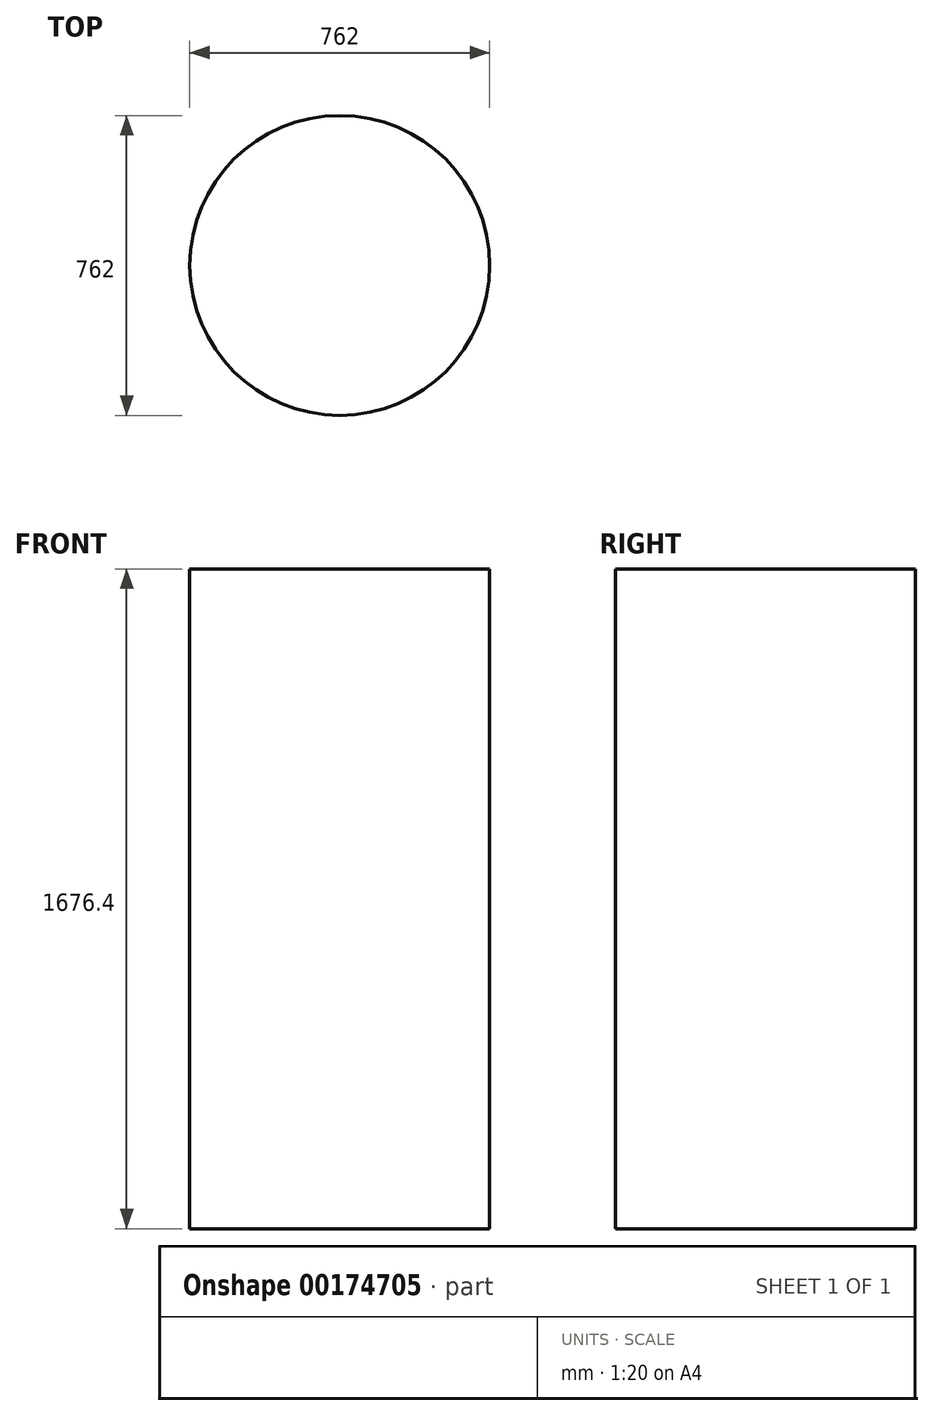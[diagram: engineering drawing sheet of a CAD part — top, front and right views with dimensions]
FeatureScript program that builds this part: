
annotation { "Feature Type Name" : "Feature", "Feature Type Description" : "" }
export const myFeature = defineFeature(function(context is Context, id is Id, definition is map)
    precondition{}
    {
        {
            var Q0;
            Q0=qCreatedBy(makeId("Top.planeOp"),FACE);
            var sketch = newSketch(context, id + "F0", { "sketchPlane" : qUnion([Q0])});
            skCircle(sketch, "E0", {"center": v(0, 0) * mm, "radius": 381 * mm});
            skSolve(sketch);
        }
        {
            var Q0;
            Q0 = qSketchRegion(id + "F0", true);
            extrude(context, id + "F1", {"entities" : qUnion([Q0]), "depth" : 1676.4 * mm});
        }
    });
